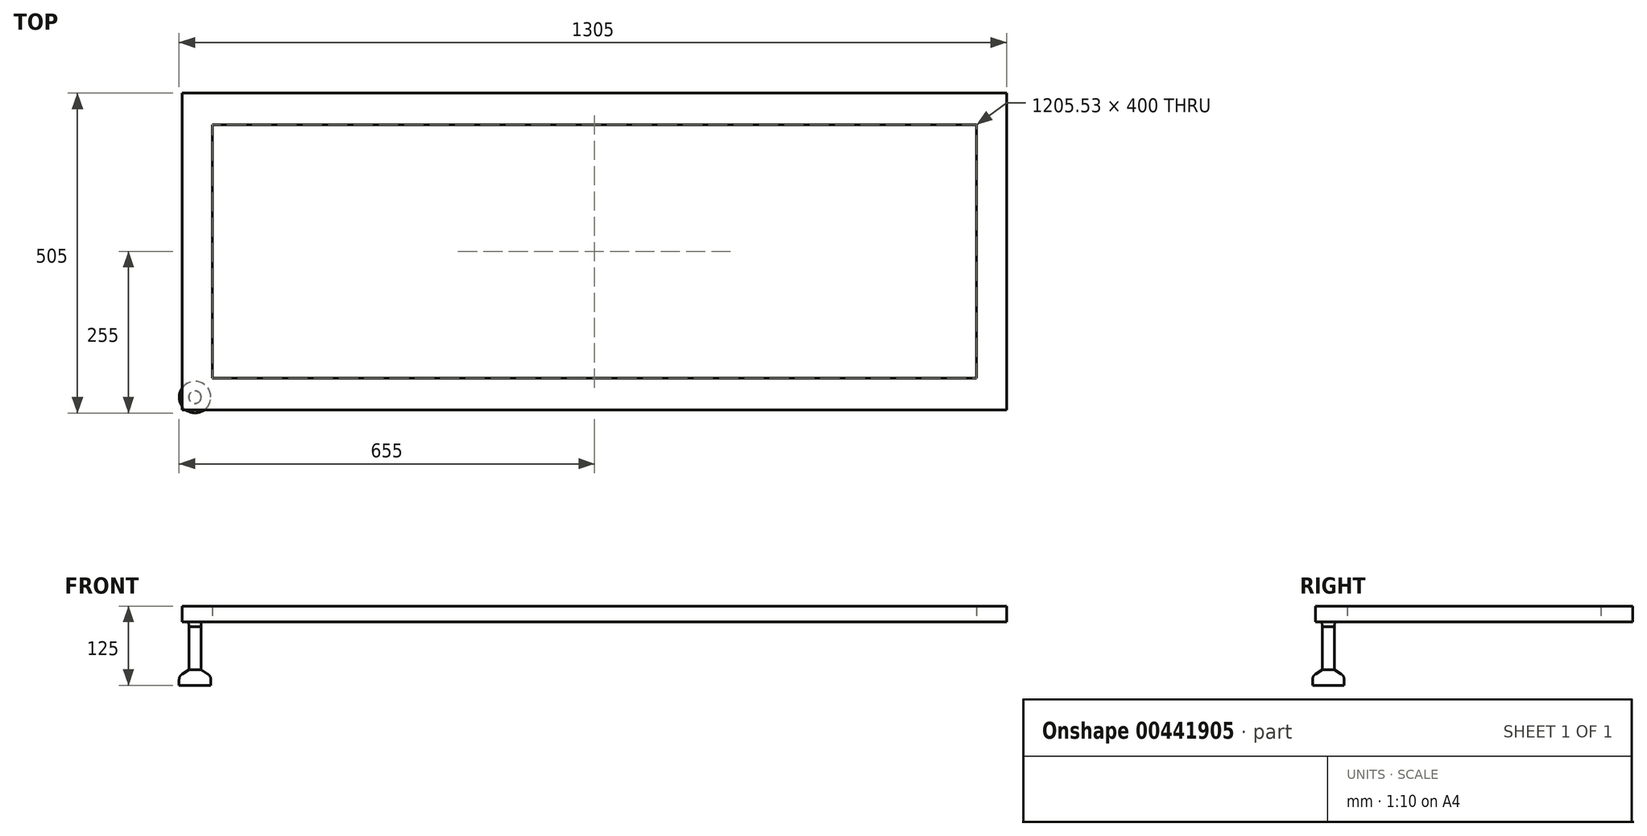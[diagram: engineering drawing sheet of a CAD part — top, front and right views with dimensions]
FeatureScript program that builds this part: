
annotation { "Feature Type Name" : "Feature", "Feature Type Description" : "" }
export const myFeature = defineFeature(function(context is Context, id is Id, definition is map)
    precondition{}
    {
        {
            var Q0;
            Q0=qCreatedBy(makeId("Top.planeOp"),FACE);
            var sketch = newSketch(context, id + "F0", { "sketchPlane" : qUnion([Q0])});
            skPoint(sketch, "E0.middle", {"position": v(0, 0) * mm});
            skLineSegment(sketch, "E1.bottom", {"start": v(650, 250) * mm, "end": v(-650, 250) * mm});
            skLineSegment(sketch, "E1.top", {"start": v(650, -250) * mm, "end": v(-650, -250) * mm});
            skLineSegment(sketch, "E1.left", {"start": v(650, 250) * mm, "end": v(650, -250) * mm});
            skLineSegment(sketch, "E1.right", {"start": v(-650, 250) * mm, "end": v(-650, -250) * mm});
            skLineSegment(sketch, "E2", {"start": v(0, 0) * mm, "end": v(-904.89, 0) * mm, "construction": true});
            skLineSegment(sketch, "E3", {"start": v(0, 0) * mm, "end": v(0, 364.48) * mm, "construction": true});
            skLineSegment(sketch, "E4", {"start": v(-630, 250) * mm, "end": v(-630, 230) * mm});
            skCircle(sketch, "E5", {"center": v(-630, 230) * mm, "radius": 10 * mm});
            skCircle(sketch, "E6.MirrorC", {"center": v(-630, -230) * mm, "radius": 10 * mm});
            skCircle(sketch, "E7.MirrorC", {"center": v(630, 230) * mm, "radius": 10 * mm});
            skCircle(sketch, "E8.MirrorC", {"center": v(630, -230) * mm, "radius": 10 * mm});
            skLineSegment(sketch, "E9.bottom", {"start": v(602.77, 200) * mm, "end": v(-602.77, 200) * mm});
            skLineSegment(sketch, "E9.top", {"start": v(602.77, -200) * mm, "end": v(-602.77, -200) * mm});
            skLineSegment(sketch, "E9.left", {"start": v(602.77, 200) * mm, "end": v(602.77, -200) * mm});
            skLineSegment(sketch, "E9.right", {"start": v(-602.77, 200) * mm, "end": v(-602.77, -200) * mm});
            skSolve(sketch);
        }
        {
            var Q0;
            Q0=qCreatedBy(makeId("Right.planeOp"),FACE);
            var sketch = newSketch(context, id + "F1", { "sketchPlane" : qUnion([Q0])});
            skLineSegment(sketch, "E10", {"start": v(0, 0) * mm, "end": v(0, -100) * mm});
            skSolve(sketch);
        }
        {
            var Q0;
            Q0=sQuery(id+"F1.wireOp",VERTEX,"E10.end");
            var Q1;
            Q1=sQuery(id+"F1.wireOp",EDGE,"E10");
            cPlane(context, id + "F2", {"entities" : qUnion([Q0, Q1]), "cplaneType" : CPlaneType.LINE_POINT, "offset" : 25 * mm, "width" : 150 * mm, "height" : 150 * mm});
        }
        {
            var Q0;
            Q0=qCreatedBy(id+"F2.planeOp",FACE);
            var sketch = newSketch(context, id + "F3", { "sketchPlane" : qUnion([Q0])});
            skCircle(sketch, "E11.0", {"center": v(-630, 230) * mm, "radius": 10 * mm});
            skPoint(sketch, "E12.0", {"position": v(-630, -230) * mm});
            skPoint(sketch, "E13.0", {"position": v(630, 230) * mm});
            skPoint(sketch, "E14.0", {"position": v(630, -230) * mm});
            skCircle(sketch, "E15", {"center": v(-630, 230) * mm, "radius": 25 * mm});
            skCircle(sketch, "E16.MirrorC", {"center": v(630, 230) * mm, "radius": 25 * mm});
            skCircle(sketch, "E17.MirrorC", {"center": v(-630, -230) * mm, "radius": 25 * mm});
            skCircle(sketch, "E18.MirrorC", {"center": v(630, -230) * mm, "radius": 25 * mm});
            skSolve(sketch);
        }
        {
            var Q0;
            Q0=sQuery(id+"F0.wireOp",EDGE,"E2");
            var Q1;
            Q1=sQuery(id+"F0.wireOp",VERTEX,"E6.MirrorC.center");
            cPlane(context, id + "F4", {"entities" : qUnion([Q0, Q1]), "cplaneType" : CPlaneType.LINE_POINT, "offset" : 25 * mm, "width" : 150 * mm, "height" : 150 * mm});
        }
        {
            var Q0;
            Q0=qCreatedBy(id+"F4.planeOp",FACE);
            var sketch = newSketch(context, id + "F5", { "sketchPlane" : qUnion([Q0])});
            skLineSegment(sketch, "E19.0", {"start": v(220, 0) * mm, "end": v(240, 0) * mm});
            skLineSegment(sketch, "E20.0", {"start": v(205, -100) * mm, "end": v(255, -100) * mm});
            skLineSegment(sketch, "E21", {"start": v(205, -100) * mm, "end": v(205, -90.83) * mm});
            skLineSegment(sketch, "E22", {"start": v(209.58, -82.43) * mm, "end": v(220.32, -75.49) * mm});
            skLineSegment(sketch, "E23", {"start": v(220.32, -75.49) * mm, "end": v(220.32, -7.53) * mm});
            skLineSegment(sketch, "E24", {"start": v(220.32, -7.53) * mm, "end": v(220, 0) * mm});
            skLineSegment(sketch, "E25", {"start": v(230, 0) * mm, "end": v(230, -114) * mm});
            skPoint(sketch, "E26.visualSharp", {"position": v(205, -85.38) * mm});
            skArc(sketch, "E26.filletArc", {"start": v(209.58, -82.43) * mm, "mid": v(206.22, -86.04) * mm, "end": v(205, -90.83) * mm});
            skSolve(sketch);
        }
        {
            var Q0;
            {var subQ0=sQuery(id+"F5.wireOp",EDGE,"E21");Q0=makeQuery(id+"F5.imprint","IMPRINT",FACE,{"disambiguationData":[TD([[makeQuery(id+"F5.imprint","IMPRINT",EDGE,{"derivedFrom":subQ0}),-1.0]])]});}
            var Q1;
            Q1=sQuery(id+"F5.wireOp",EDGE,"E25");
            revolve(context, id + "F6", {"entities" : qUnion([Q0]), "axis" : qUnion([Q1]), "revolveType" : RevolveType.FULL});
        }
        {
            var Q0;
            Q0=makeQuery(id+"F0.imprint","IMPRINT",FACE,{"disambiguationData":[TD([[makeQuery(id+"F0.imprint","IMPRINT",EDGE,{"derivedFrom":sQuery(id+"F0.wireOp",EDGE,"E1.top")}),-1.0]])]});
            var sketch = newSketch(context, id + "F7", { "sketchPlane" : qUnion([Q0])});
            skLineSegment(sketch, "E27.0.0", {"start": v(-602.77, -200) * mm, "end": v(602.77, -200) * mm});
            skLineSegment(sketch, "E27.0.1", {"start": v(602.77, -200) * mm, "end": v(602.77, 200) * mm});
            skLineSegment(sketch, "E27.0.2", {"start": v(602.77, 200) * mm, "end": v(-602.77, 200) * mm});
            skLineSegment(sketch, "E27.0.3", {"start": v(-602.77, 200) * mm, "end": v(-602.77, -200) * mm});
            skLineSegment(sketch, "E28.0", {"start": v(-650, 250) * mm, "end": v(-650, -250) * mm});
            skLineSegment(sketch, "E29.0", {"start": v(650, 250) * mm, "end": v(-650, 250) * mm});
            skLineSegment(sketch, "E30.0", {"start": v(650, 250) * mm, "end": v(650, -250) * mm});
            skLineSegment(sketch, "E31.0", {"start": v(650, -250) * mm, "end": v(-650, -250) * mm});
            skSolve(sketch);
        }
        {
            var Q0;
            Q0 = qSketchRegion(id + "F7", true);
            extrude(context, id + "F8", {"entities" : qUnion([Q0]), "depth" : 25 * mm});
        }
    });
